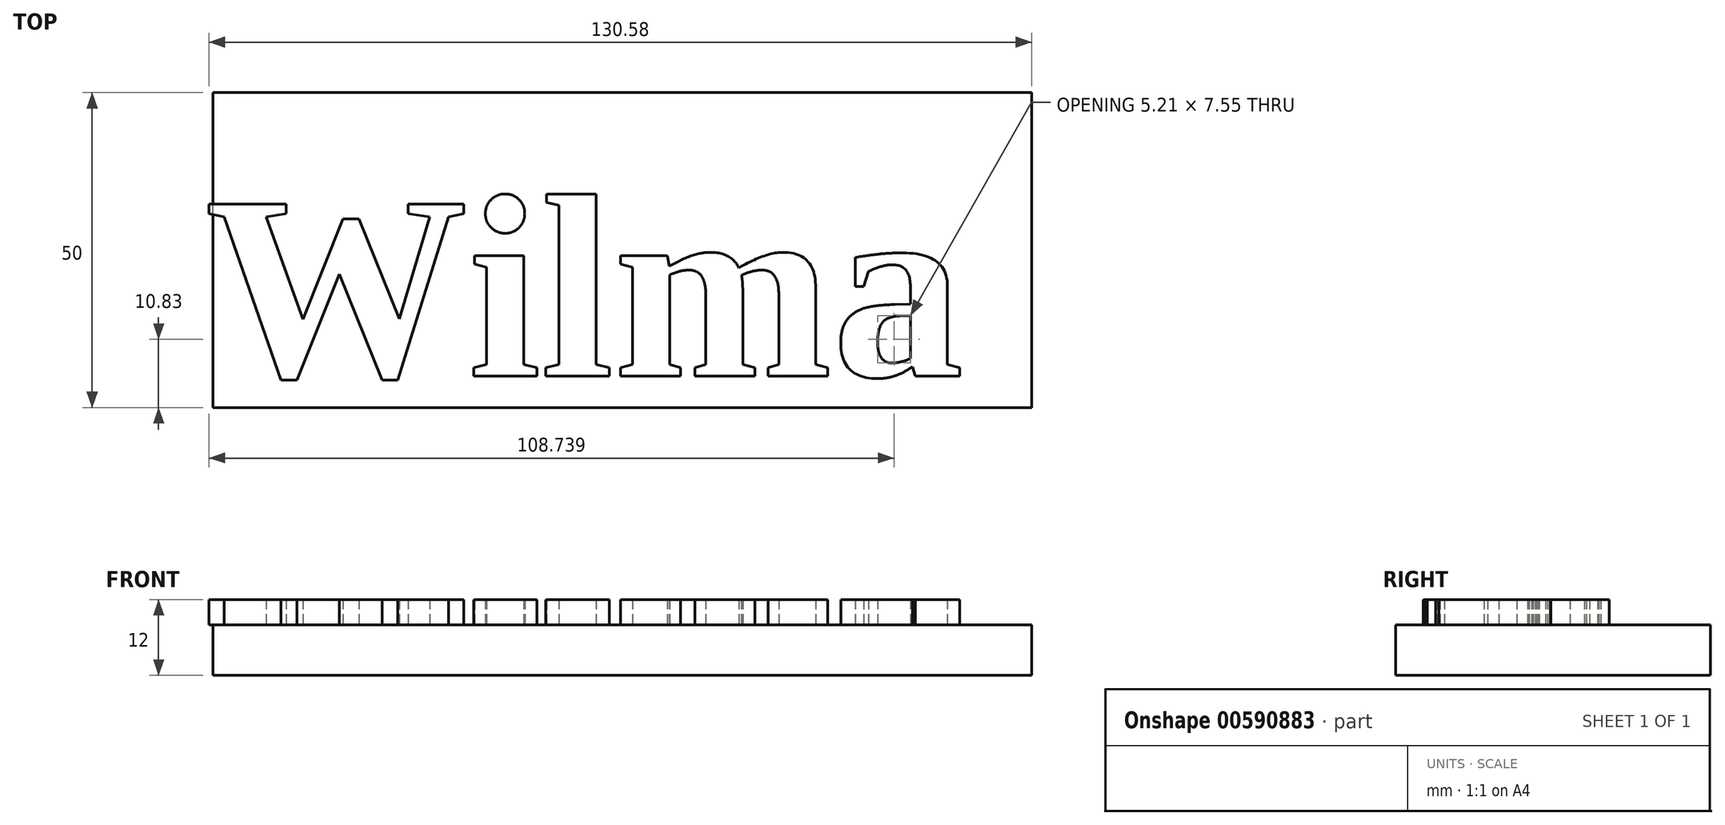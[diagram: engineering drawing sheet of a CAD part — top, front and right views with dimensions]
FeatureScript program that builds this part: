
annotation { "Feature Type Name" : "Feature", "Feature Type Description" : "" }
export const myFeature = defineFeature(function(context is Context, id is Id, definition is map)
    precondition{}
    {
        {
            var Q0;
            Q0=qCreatedBy(makeId("Top.planeOp"),FACE);
            var sketch = newSketch(context, id + "F0", { "sketchPlane" : qUnion([Q0])});
            skLineSegment(sketch, "E0.bottom", {"start": v(0, 0) * mm, "end": v(130, 0) * mm});
            skLineSegment(sketch, "E0.top", {"start": v(0, 50) * mm, "end": v(130, 50) * mm});
            skLineSegment(sketch, "E0.left", {"start": v(0, 0) * mm, "end": v(0, 50) * mm});
            skLineSegment(sketch, "E0.right", {"start": v(130, 0) * mm, "end": v(130, 50) * mm});
            skSolve(sketch);
        }
        {
            var Q0;
            Q0=qSketchRegion(id+"F0",true);
            extrude(context, id + "F1", {"entities" : qUnion([Q0]), "depth" : 8 * mm, "offsetDistance" : 25 * mm});
        }
        {
            var Q0;
            Q0=makeQuery(id+"F1.opExtrude","CAP_FACE",FACE,{"disambiguationData":[OSD([sQuery(id+"F0.wireOp",EDGE,"E0.bottom"),sQuery(id+"F0.wireOp",EDGE,"E0.top"),sQuery(id+"F0.wireOp",EDGE,"E0.left"),sQuery(id+"F0.wireOp",EDGE,"E0.right")])],"isStart":false});
            var sketch = newSketch(context, id + "F2", { "sketchPlane" : qUnion([Q0])});
            skText(sketch, "E1", { "text": "Wilma", "fontName": "Tinos-Bold.ttf"});
            skLineSegment(sketch, "E2", {"start": v(65, 50) * mm, "end": v(65, 0) * mm, "construction": true});
            skLineSegment(sketch, "E3", {"start": v(0, 25) * mm, "end": v(130, 25) * mm, "construction": true});
            skLineSegment(sketch, "E4", {"start": v(3.83, 25) * mm, "end": v(126.17, 25) * mm, "construction": true});
            const initialGuessF2  = {"E1": [-0.00117, 0.005, 1, 0, 0.03]};
            skSetInitialGuess(sketch, initialGuessF2);
            skSolve(sketch);
        }
        {
            var Q0;
            Q0=qSketchRegion(id+"F2",true);
            extrude(context, id + "F3", {"entities" : qUnion([Q0]), "depth" : 4 * mm, "offsetDistance" : 25 * mm});
        }
    });
